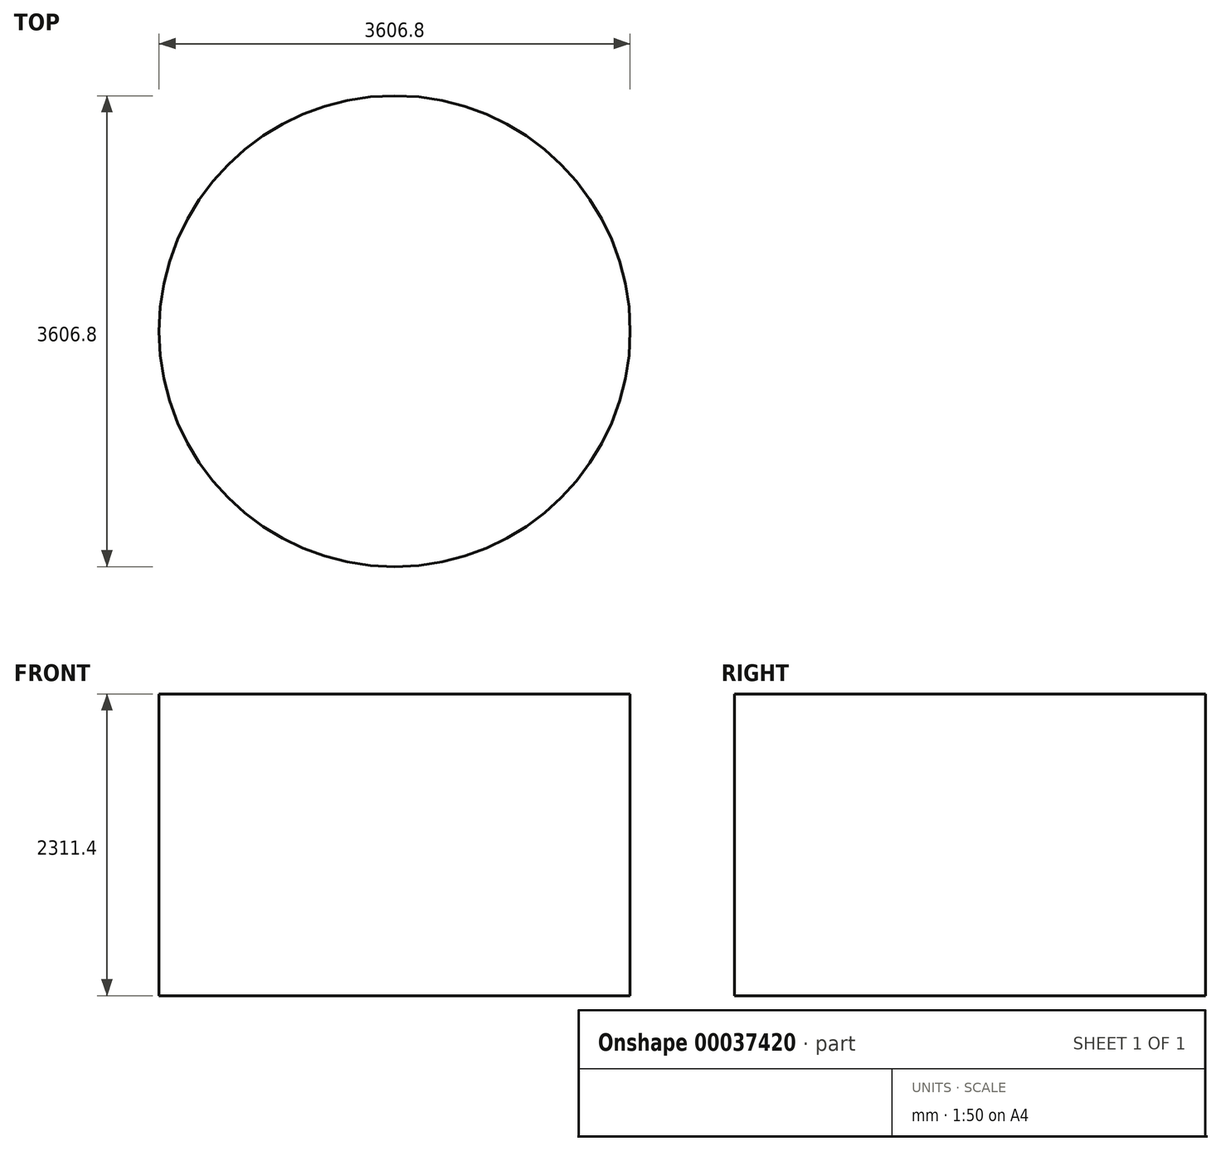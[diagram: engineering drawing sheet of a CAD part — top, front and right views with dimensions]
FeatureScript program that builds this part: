
annotation { "Feature Type Name" : "Feature", "Feature Type Description" : "" }
export const myFeature = defineFeature(function(context is Context, id is Id, definition is map)
    precondition{}
    {
        {
            var Q0;
            Q0=qCreatedBy(makeId("Top.planeOp"),FACE);
            var sketch = newSketch(context, id + "F0", { "sketchPlane" : qUnion([Q0])});
            skCircle(sketch, "E0", {"center": v(-2413, 0) * mm, "radius": 1803.4 * mm});
            skLineSegment(sketch, "E1", {"start": v(-609.6, 0) * mm, "end": v(0, 0) * mm, "construction": true});
            skLineSegment(sketch, "E2", {"start": v(0, 0) * mm, "end": v(0, 2413) * mm});
            skLineSegment(sketch, "E3", {"start": v(0, 2413) * mm, "end": v(-4267.2, 2413) * mm});
            skLineSegment(sketch, "E4", {"start": v(-4267.2, 2413) * mm, "end": v(-4267.2, -926.98) * mm});
            skCircle(sketch, "E5", {"center": v(-1016, 2082.8) * mm, "radius": 330.2 * mm});
            skLineSegment(sketch, "E6.bottom", {"start": v(-425.34, 1324.03) * mm, "end": v(-272.94, 1324.03) * mm});
            skLineSegment(sketch, "E6.top", {"start": v(-425.34, 638.23) * mm, "end": v(-272.94, 638.23) * mm});
            skLineSegment(sketch, "E6.left", {"start": v(-425.34, 1324.03) * mm, "end": v(-425.34, 638.23) * mm});
            skLineSegment(sketch, "E6.right", {"start": v(-272.94, 1324.03) * mm, "end": v(-272.94, 638.23) * mm});
            skCircle(sketch, "E7", {"center": v(-330.2, 2082.8) * mm, "radius": 330.2 * mm});
            skLineSegment(sketch, "E8", {"start": v(-1016, 1752.6) * mm, "end": v(-1016, 1485.9) * mm});
            skLineSegment(sketch, "E9", {"start": v(-330.2, 1752.6) * mm, "end": v(-330.2, 1485.9) * mm});
            skLineSegment(sketch, "E10", {"start": v(-1016, 1485.9) * mm, "end": v(-330.2, 1485.9) * mm});
            skSolve(sketch);
        }
        {
            var Q0;
            Q0=makeQuery(id+"F0.imprint","IMPRINT",FACE,{"disambiguationData":[TD([[makeQuery(id+"F0.imprint","IMPRINT",EDGE,{"derivedFrom":sQuery(id+"F0.wireOp",EDGE,"E0")}),1.0]])]});
            extrude(context, id + "F1", {"entities" : qUnion([Q0]), "depth" : 2311.4 * mm});
        }
    });
